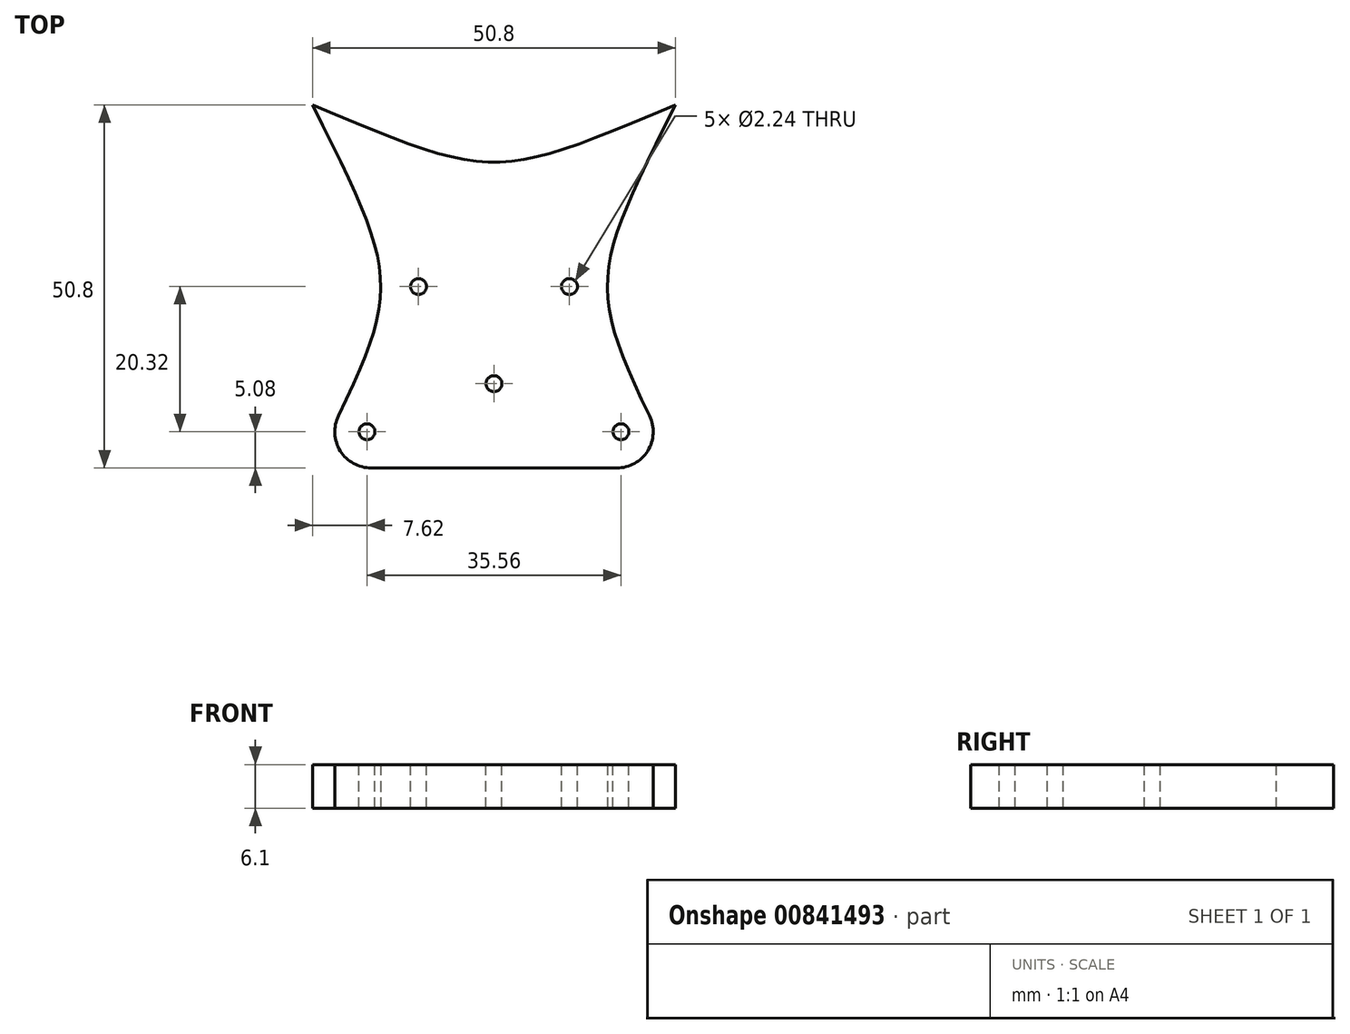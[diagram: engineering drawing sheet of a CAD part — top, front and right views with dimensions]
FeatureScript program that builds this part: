
annotation { "Feature Type Name" : "Feature", "Feature Type Description" : "" }
export const myFeature = defineFeature(function(context is Context, id is Id, definition is map)
    precondition{}
    {
        {
            var Q0;
            Q0=qCreatedBy(makeId("Top.planeOp"),FACE);
            var sketch = newSketch(context, id + "F0", { "sketchPlane" : qUnion([Q0])});
            skFitSpline(sketch, "E0", {"points": [v(-25.4, 25.4) * mm, v(-25.4, -25.4) * mm], "startDerivative": vector(38.1, -76.23) * mm, "endDerivative": vector(-38.16, -76.2) * mm});
            skFitSpline(sketch, "E1", {"points": [v(25.4, 25.4) * mm, v(25.4, -25.4) * mm], "startDerivative": vector(-38.1, -76.2) * mm, "endDerivative": vector(38.1, -76.2) * mm});
            skFitSpline(sketch, "E2", {"points": [v(-25.4, 25.4) * mm, v(25.4, 25.4) * mm], "startDerivative": vector(76.2, -31.93) * mm, "endDerivative": vector(76.2, 31.93) * mm});
            skLineSegment(sketch, "E3", {"start": v(-25.4, -25.4) * mm, "end": v(25.4, -25.4) * mm});
            skSolve(sketch);
        }
        {
            var Q0;
            Q0 = qSketchRegion(id + "F0", true);
            extrude(context, id + "F1", {"entities" : qUnion([Q0]), "endBound" : BoundingType.SYMMETRIC, "depth" : 6.1 * mm, "offsetDistance" : 25.4 * mm});
        }
        {
            var Q0;
            Q0=makeQuery(id+"F1.opExtrude","CAP_FACE",FACE,{"disambiguationData":[OSD([sQuery(id+"F0.wireOp",EDGE,"E0"),sQuery(id+"F0.wireOp",EDGE,"E1"),sQuery(id+"F0.wireOp",EDGE,"e48b32bf-107a-4277-9766-09f134d8dee1"),sQuery(id+"F0.wireOp",EDGE,"E2")])],"isStart":false});
            var sketch = newSketch(context, id + "F2", { "sketchPlane" : qUnion([Q0])});
            skCircle(sketch, "E4", {"center": v(-17.78, -20.32) * mm, "radius": 1.12 * mm});
            skCircle(sketch, "E5", {"center": v(17.78, -20.32) * mm, "radius": 1.12 * mm});
            skCircle(sketch, "E6", {"center": v(0, -13.6) * mm, "radius": 1.12 * mm});
            skCircle(sketch, "E7", {"center": v(-10.57, 0) * mm, "radius": 1.12 * mm});
            skCircle(sketch, "E8.MirrorC", {"center": v(10.57, 0) * mm, "radius": 1.12 * mm});
            skSolve(sketch);
        }
        {
            var Q0;
            Q0 = qSketchRegion(id + "F2", true);
            extrude(context, id + "F3", {"entities" : qUnion([Q0]), "operationType" : NewBodyOperationType.REMOVE, "oppositeDirection" : true, "depth" : 6.35 * mm, "offsetDistance" : 25.4 * mm});
        }
        {
            var Q0;
            Q0=makeQuery(id+"F1.opExtrude","SWEPT_EDGE",EDGE,{"disambiguationData":[OSD([sQuery(id+"F0.wireOp",EDGE,"E0"),sQuery(id+"F0.wireOp",EDGE,"E3")])]});
            var Q1;
            Q1=makeQuery(id+"F1.opExtrude","SWEPT_EDGE",EDGE,{"disambiguationData":[OSD([sQuery(id+"F0.wireOp",EDGE,"E1"),sQuery(id+"F0.wireOp",EDGE,"E3")])]});
            fillet(context, id + "F4", {"entities" : qUnion([Q0, Q1]), "radius" : 5.08 * mm, "tangentPropagation" : true, "allowEdgeOverflow" : false});
        }
    });
